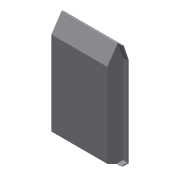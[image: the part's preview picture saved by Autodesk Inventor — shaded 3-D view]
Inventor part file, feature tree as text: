
AUTODESK INVENTOR PART (.ipt)
format: ipt  version: 2015 (Build 190159000, 159)  size: 92,160 bytes
history: native  units: mm
features: sketch x3, extrude x2
ambient origin geometry x8: Origin, YZ Plane, XZ Plane, XY Plane, X Axis, Y Axis, Z Axis, Center Point
bodies: Solid1 (feature_tree)
feature tree (5):
  extrude  "Extrusion1"  Depth=30.0mm
  extrude  "Extrusion2"  Depth=2.0mm
  sketch  "Sketch3"  dims[d9=8.0mm d10=0.0mm]
  sketch  "Sketch1"  dims[d0=150.0mm d4=30.0mm]
  sketch  "Sketch2"  dims[d5=100.0mm d6=0.0mm d7=2.0mm]
